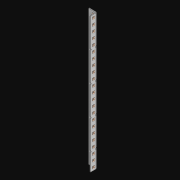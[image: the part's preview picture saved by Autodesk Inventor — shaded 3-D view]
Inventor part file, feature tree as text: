
AUTODESK INVENTOR PART (.ipt)
format: ipt  version: 2021 (Build 250183000, 183)  size: 1,243,648 bytes
history: native  units: in
note: dims shown in document units (in); Inventor stores cm internally (conversion verified against a paired STEP export)
features: extrude x48, other x46, sketch x4, pattern_linear x2, sheet_metal_op x1
ambient origin geometry x8: Origin, YZ Plane, XZ Plane, XY Plane, X Axis, Y Axis, Z Axis, Center Point
bodies: Solid1 (feature_tree)
feature tree (101):
  pattern_linear  "Rectangular Pattern1"  Spacing1=0.5in  [1 undecoded]
  pattern_linear  "Rectangular Pattern3"  Count1=23  [1 undecoded]
  extrude  "Extrusion1"  Depth=0.5in
  extrude  "Extrusion2"  Depth=0.5in
  sketch  "Sketch1"  dims[d0=0.182in]
  other  "Srf1"
  sketch  "Sketch3"  dims[d1=0.063in d2=0.0in]
  other  "Srf3"
  other  "Srf4"
  other  "Srf5"
  other  "Srf6"
  other  "Srf7"
  other  "Srf8"
  other  "Srf9"
  other  "Srf10"
  other  "Srf11"
  other  "Srf12"
  other  "Srf13"
  other  "Srf14"
  other  "Srf15"
  other  "Srf16"
  other  "Srf17"
  other  "Srf18"
  other  "Srf19"
  other  "Srf20"
  other  "Srf21"
  other  "Srf22"
  other  "Srf23"
  other  "Srf24"
  other  "Srf25"
  other  "Srf142"
  other  "Srf143"
  other  "Srf144"
  other  "Srf145"
  other  "Srf146"
  other  "Srf147"
  other  "Srf148"
  other  "Srf149"
  other  "Srf150"
  other  "Srf151"
  other  "Srf152"
  other  "Srf153"
  other  "Srf154"
  other  "Srf155"
  other  "Srf156"
  other  "Srf157"
  other  "Srf158"
  other  "Srf159"
  other  "Srf160"
  other  "Srf161"
  other  "Srf162"
  other  "Srf163"
  sketch  "Sketch4"  dims[d6=0.182in]
  sketch  "Sketch5"  dims[d7=0.063in d8=0.0in d11=0.5in d12=0.3937in d14=0.5in d18=9.0551in d20=0.5in d21=6.0in d22=0.0in d23=0.841in d24=0.0in]
  sheet_metal_op  "Fold1"
  extrude  "ExtrusionSrf1"  TaperAngle=0.0deg  [1 undecoded]
  extrude  "ExtrusionSrf3"  Depth=0.5in TaperAngle=0.0deg
  extrude  "ExtrusionSrf4"  [1 undecoded]
  extrude  "ExtrusionSrf5"  [1 undecoded]
  extrude  "ExtrusionSrf6"  [1 undecoded]
  extrude  "ExtrusionSrf7"  [1 undecoded]
  extrude  "ExtrusionSrf8"  [1 undecoded]
  extrude  "ExtrusionSrf9"  [1 undecoded]
  extrude  "ExtrusionSrf10"  [1 undecoded]
  extrude  "ExtrusionSrf11"  [1 undecoded]
  extrude  "ExtrusionSrf12"  [1 undecoded]
  extrude  "ExtrusionSrf13"  [1 undecoded]
  extrude  "ExtrusionSrf14"  [1 undecoded]
  extrude  "ExtrusionSrf15"  [1 undecoded]
  extrude  "ExtrusionSrf16"  [1 undecoded]
  extrude  "ExtrusionSrf17"  [1 undecoded]
  extrude  "ExtrusionSrf18"  [1 undecoded]
  extrude  "ExtrusionSrf19"  [1 undecoded]
  extrude  "ExtrusionSrf20"  [1 undecoded]
  extrude  "ExtrusionSrf21"  [1 undecoded]
  extrude  "ExtrusionSrf22"  [1 undecoded]
  extrude  "ExtrusionSrf23"  [1 undecoded]
  extrude  "ExtrusionSrf24"  [1 undecoded]
  extrude  "ExtrusionSrf25"  [1 undecoded]
  extrude  "ExtrusionSrf142"  [1 undecoded]
  extrude  "ExtrusionSrf143"  [1 undecoded]
  extrude  "ExtrusionSrf144"  [1 undecoded]
  extrude  "ExtrusionSrf145"  [1 undecoded]
  extrude  "ExtrusionSrf146"  [1 undecoded]
  extrude  "ExtrusionSrf147"  [1 undecoded]
  extrude  "ExtrusionSrf148"  [1 undecoded]
  extrude  "ExtrusionSrf149"  [1 undecoded]
  extrude  "ExtrusionSrf150"  [1 undecoded]
  extrude  "ExtrusionSrf151"  [1 undecoded]
  extrude  "ExtrusionSrf152"  [1 undecoded]
  extrude  "ExtrusionSrf153"  [1 undecoded]
  extrude  "ExtrusionSrf154"  [1 undecoded]
  extrude  "ExtrusionSrf155"  [1 undecoded]
  extrude  "ExtrusionSrf156"  [1 undecoded]
  extrude  "ExtrusionSrf157"  [1 undecoded]
  extrude  "ExtrusionSrf158"  [1 undecoded]
  extrude  "ExtrusionSrf159"  [1 undecoded]
  extrude  "ExtrusionSrf160"  [1 undecoded]
  extrude  "ExtrusionSrf161"  [1 undecoded]
  extrude  "ExtrusionSrf162"  [1 undecoded]
  extrude  "ExtrusionSrf163"  [1 undecoded]
note: 47 required parameter values undecoded (feature->parameter linkage not recoverable at this tier; creation-order binding heuristic only, values carry confidence <= 0.55)
